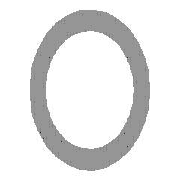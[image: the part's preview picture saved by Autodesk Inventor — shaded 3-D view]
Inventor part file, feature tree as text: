
AUTODESK INVENTOR PART (.ipt)
format: ipt  version: 2017 (Build 210142000, 142)  size: 117,248 bytes
history: native  units: mm (DEFAULTED — no unit token found)
features: other x3, sketch x3, plane x1
ambient origin geometry x8: Origin, YZ Plane, XZ Plane, XY Plane, X Axis, Y Axis, Z Axis, Center Point
bodies: Solid1 (feature_tree), Body (feature_tree)
feature tree (7):
  other  "Driven Length"
  other  "Start plane"
  other  "End plane"
  sketch  "Sketch"  dims[d2=258.5mm d3=0.0mm d4=-0.0mm d5=258.5mm d6=90.0deg d7=258.5mm]
  sketch  "Sketch3"  dims[d0=25.0mm]
  plane  "Work Plane3"
  sketch  "Sketch4"  dims[d1=1.5mm]
